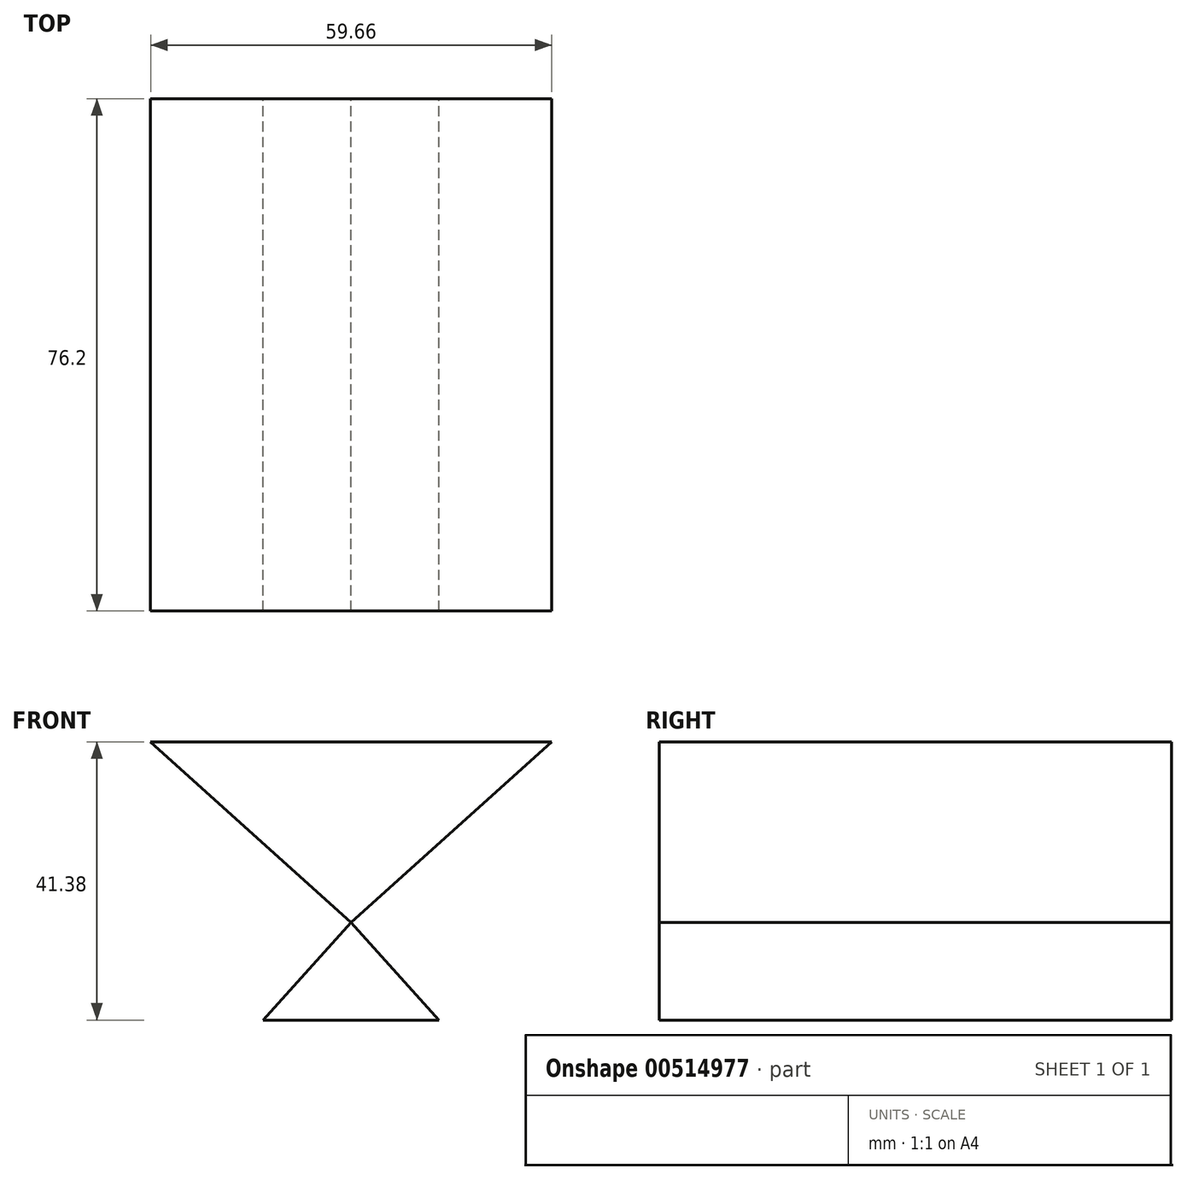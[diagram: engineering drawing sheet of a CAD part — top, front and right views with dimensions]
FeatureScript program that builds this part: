
annotation { "Feature Type Name" : "Feature", "Feature Type Description" : "" }
export const myFeature = defineFeature(function(context is Context, id is Id, definition is map)
    precondition{}
    {
        {
            var Q0;
            Q0=qCreatedBy(makeId("Front.planeOp"),FACE);
            var sketch = newSketch(context, id + "F0", { "sketchPlane" : qUnion([Q0])});
            skLineSegment(sketch, "E0", {"start": v(-13.08, 0) * mm, "end": v(13.08, 0) * mm});
            skLineSegment(sketch, "E1", {"start": v(-13.08, 0) * mm, "end": v(0, 14.54) * mm});
            skLineSegment(sketch, "E2", {"start": v(0, 14.54) * mm, "end": v(13.08, 0) * mm});
            skLineSegment(sketch, "E3", {"start": v(0, 14.54) * mm, "end": v(29.83, 41.38) * mm});
            skLineSegment(sketch, "E4", {"start": v(0, 14.54) * mm, "end": v(-29.83, 41.38) * mm});
            skLineSegment(sketch, "E5", {"start": v(-29.83, 41.38) * mm, "end": v(29.83, 41.38) * mm});
            skSolve(sketch);
        }
        {
            var Q0;
            Q0 = qSketchRegion(id + "F0", true);
            extrude(context, id + "F1", {"entities" : qUnion([Q0]), "depth" : 76.2 * mm, "offsetDistance" : 25.4 * mm});
        }
    });
